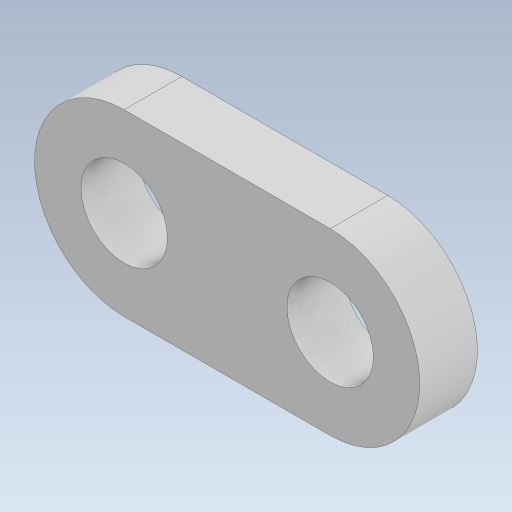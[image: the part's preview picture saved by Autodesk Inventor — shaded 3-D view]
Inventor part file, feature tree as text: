
AUTODESK INVENTOR PART (.ipt)
format: ipt  version: 2023 (Build 270158000, 158)  size: 299,008 bytes
history: native  units: in
note: dims shown in document units (in); Inventor stores cm internally (conversion verified against a paired STEP export)
features: sketch x2, extrude x1, hole x1, fillet x1
ambient origin geometry x8: Origin, YZ Plane, XZ Plane, XY Plane, X Axis, Y Axis, Z Axis, Center Point
bodies: Solid1 (feature_tree)
feature tree (5):
  extrude  "Extrusion1"  Depth=0.1772in
  hole  "Hole1"  [1 undecoded]
  fillet  "Fillet1"  Radius=0.5512in
  sketch  "Sketch2"  dims[d7=0.6339in d8=0.1772in]
  sketch  "Sketch3"  dims[d9=0.2756in d11=0.2756in d12=0.5512in d13=0.0in d16=0.266in d17=0.2362in d18=0.507in d19=0.0787in d20=0.5635in d21=0.1969in d22=0.8108in d23=0.2756in]
note: 1 required parameter value undecoded (feature->parameter linkage not recoverable at this tier; creation-order binding heuristic only, values carry confidence <= 0.55)
